# Revit family: Indoor 140 types Sans hôte
name_source: partatom
category: Dispositifs d'éclairage
units: mm (PartAtom-declared; Revit-internal decimal feet)

## family parameters
Basée sur le plan de construction = Non
Conserver l'orientation des annotations = Non
Cote de connecteur circulaire = Utiliser le diamètre
Couper avec des vides une fois chargée = Non
Partagée = Non
Point de calcul de pièce = Non
Toujours verticalement = Oui
Type d'élément = Normal

## types (4) — shared parameters
Classe = II
Code d'assemblage = D5010200
Elévation par défaut = 110 cm
Fabricant = B.E.G.
Hauteur de montage max = 220 cm
IP = 20
Image du type = MURAL.JPG
Marque = LUXOMAT
Mode de pose = Encastré mural
Position en hauteur = 110 cm
URL = http://www.luxomat.com

## per-type parameters (varying)
| type | Alimentation | Charge Cos ɸ =0.5 | Charge Cos ɸ =1 | Charge LED | Commentaires du type | Consommation | Modèle | Relais | Référence | Température ambiante | Type de Sortie |
| 01- INDOOR 140 EN Générique | 110-240 V AC |  |  |  | INTER.AUTO.BALISAGE LED INTEGRE.120°/8M ENCASTRE MURAL |  | INDOOR 140 EN |  |  | -25°C à + 50°C |  |
| 02- INDOOR 140 L EN réf 94328 | 110-240 V AC | 1000 VA | 2000 W | 250 W | INTER.AUTO.3 FILS.1 CONTACT.BALISAGE LED INTEGRE.120°/8M ENCASTRE MURAL | 0.4 à 0.8 W | INDOOR 140 EN | 10 A | 94328 | -25°C à + 50°C | TOR + balisage LED intégré |
| 03- INDOOR 140 L KNX DX EN réf 93393 | 24 V DC par bus KNX | 0 | 0 | 0 | INTER.AUTO.KNX.VERSION DELUXE.BALISAGE LED INTEGRE.120°/8M ENCASTRE MURAL | 12 mA | INDOOR 140 KNX DX EN | 0 | 93393 | -5°C à + 45°C | KNX - 1 sortie Eclairage TOR ou GRADATION / 3 sorties Présence / Capteur de température |
| 04- INDOOR 140 L KNXs DX EN réf 93526 | 24 V DC par bus KNX | 0 | 0 | 0 | INTER.AUTO.KNX SECURE.VERSION DELUXE.BALISAGE LED INTEGRE.120°/8M ENCASTRE MURAL | 12 mA | INDOOR 140 KNXs DX EN | 0 | 93526 | -5°C à + 45°C | KNX Sécure - 1 sortie Eclairage TOR ou GRADATION / 3 sorties Présence / Capteur de température / HCL |
